SOLIDWORKS PART (.sldprt)
format: sldprt  version: not decoded by parser v0  size: 137,216 bytes
history: native  units: mm
features: sketch x5, cut_extrude x3, extrude x2, material x1 (+13 scaffold rows collapsed)
feature tree (24):
  scaffold x13  (default folders/planes/origin — collapsed)
  material  "Material <not specified>"
  sketch  "Sketch1"  dims[D1=6.35mm D2=44.45mm]
  extrude  "Boss-Extrude1"  Depth=25.4mm
  sketch  "Sketch2"  dims[D1=10.16mm D2=8.89mm]
  extrude  "Boss-Extrude2"  Depth=7.112mm
  sketch  "Sketch3"  dims[D1=0.0254mm]
  sketch  "Sketch4"
  cut_extrude  "Cut-Extrude1"  [1 undecoded]
  cut_extrude  "Cut-Extrude2"  [1 undecoded]
  sketch  "Sketch5"  dims[D1=0.127mm]
  cut_extrude  "Cut-Extrude3"  [1 undecoded]
decode coverage: 6 of 10 modeling features carry decoded parameters
note: 3 parameter values undecoded
summary: no parameter record found for 3 features
note: suppression state not decoded; provenance and decode notes live in map.json
